FCSTD DOCUMENT  (FreeCAD 0.18R4 (GitTag))
Label: FreeCADTutorial2
License: All rights reserved
LicenseURL: http://en.wikipedia.org/wiki/All_rights_reserved
objects: Sketcher::SketchObject×1
note: 1 computed .brp shape members not serialized (recipe doc carries the construction recipe); baked Part::Feature solids carry a one-line shape summary decoded from their .brp

FEATURE [Sketcher::SketchObject] Sketch
  sketch-geometry (4):
    g0: LineSegment StartX=14.6672 StartY=62.3548 StartZ=0 EndX=50.4651 EndY=62.3548 EndZ=0
    g1: LineSegment StartX=50.4651 StartY=62.3548 StartZ=0 EndX=50.3339 EndY=24.8851 EndZ=0
    g2: ArcOfCircle CenterX=32.4023 CenterY=24.9479 CenterZ=0 NormalX=0 NormalY=0 NormalZ=1 AngleXU=0 Radius=17.9318 StartAngle=3.13633 EndAngle=6.27968
    g3: LineSegment StartX=14.4707 StartY=25.0422 StartZ=0 EndX=14.6672 EndY=62.3548 EndZ=0
  constraints (6):
    c: Coincident(g0,g1)
    c: Tangent(g1,g2) = 1.5708
    c: Tangent(g2,g3) = 1.5708
    c: Coincident(g3,g0)
    c: Horizontal(g0)
    c: Distance(g1) = 37.47
